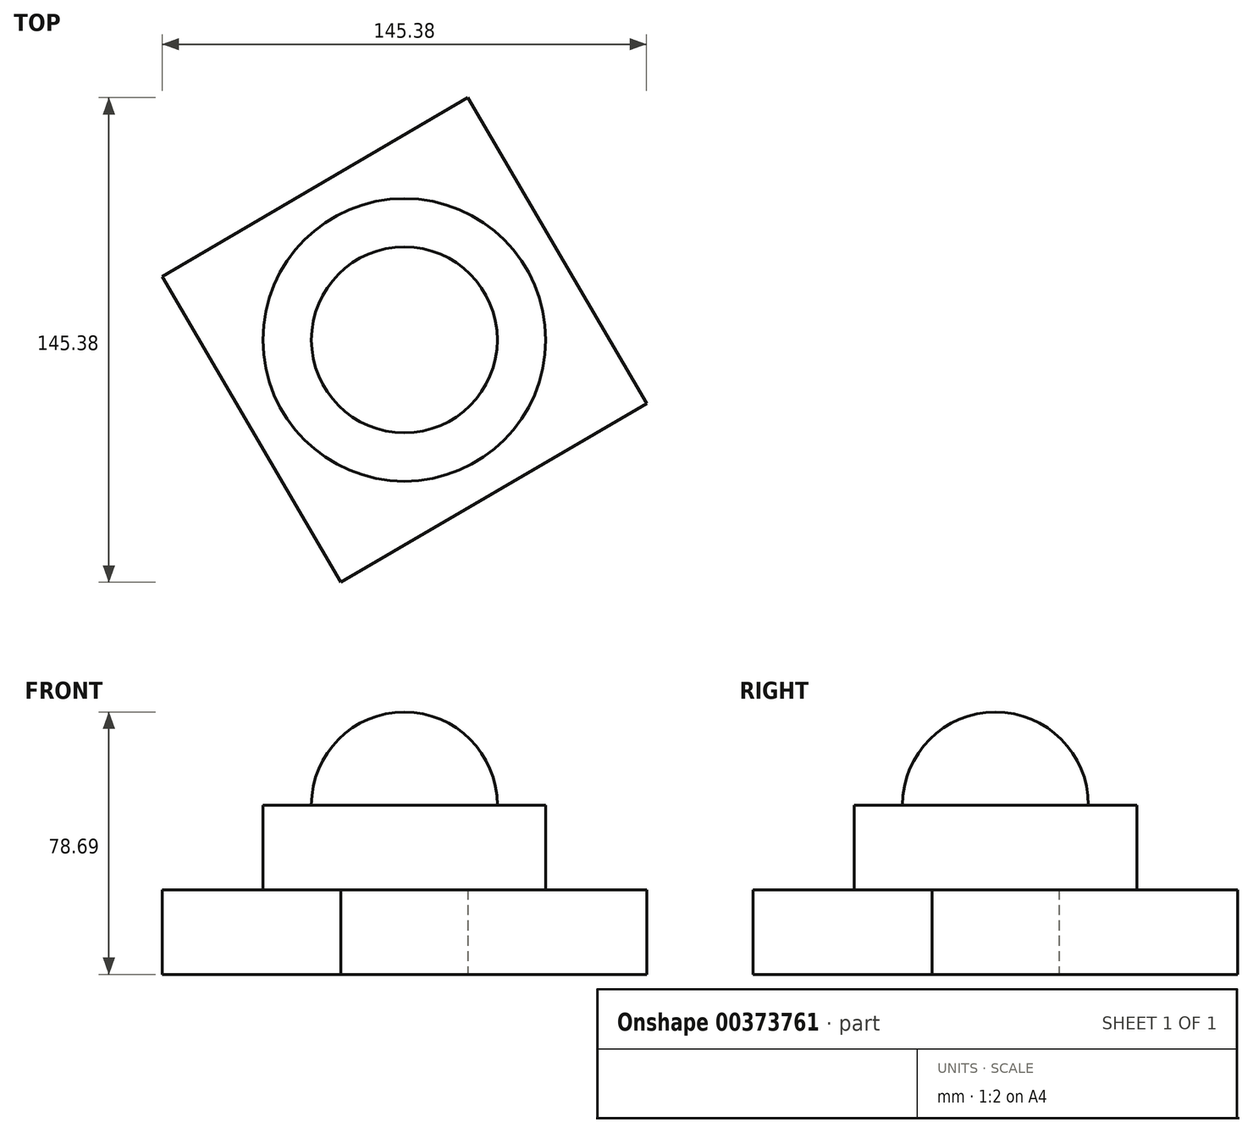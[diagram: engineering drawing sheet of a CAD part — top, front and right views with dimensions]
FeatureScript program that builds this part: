
annotation { "Feature Type Name" : "Feature", "Feature Type Description" : "" }
export const myFeature = defineFeature(function(context is Context, id is Id, definition is map)
    precondition{}
    {
        {
            var Q0;
            Q0=qCreatedBy(makeId("Top.planeOp"),FACE);
            var sketch = newSketch(context, id + "F0", { "sketchPlane" : qUnion([Q0])});
            skCircle(sketch, "E0.cCircle", {"center": v(0, 0) * mm, "radius": 53.14 * mm, "construction": true});
            skLineSegment(sketch, "E0.0", {"start": v(-72.7, 19.05) * mm, "end": v(19.05, 72.7) * mm});
            skLineSegment(sketch, "E0.1", {"start": v(19.05, 72.7) * mm, "end": v(72.7, -19.05) * mm});
            skLineSegment(sketch, "E0.2", {"start": v(72.7, -19.05) * mm, "end": v(-19.05, -72.7) * mm});
            skLineSegment(sketch, "E0.3", {"start": v(-19.05, -72.7) * mm, "end": v(-72.7, 19.05) * mm});
            skPoint(sketch, "E0.0.midPoint", {"position": v(-26.82, 45.87) * mm});
            skSolve(sketch);
        }
        {
            var Q0;
            Q0 = qSketchRegion(id + "F0", true);
            extrude(context, id + "F1", {"entities" : qUnion([Q0]), "depth" : 25.4 * mm});
        }
        {
            var Q0;
            Q0=makeQuery(id+"F1.opExtrude","CAP_FACE",FACE,{"disambiguationData":[OSD([sQuery(id+"F0.wireOp",EDGE,"E0.0"),sQuery(id+"F0.wireOp",EDGE,"E0.1"),sQuery(id+"F0.wireOp",EDGE,"E0.2"),sQuery(id+"F0.wireOp",EDGE,"E0.3")])],"isStart":false});
            var sketch = newSketch(context, id + "F2", { "sketchPlane" : qUnion([Q0])});
            skCircle(sketch, "E1", {"center": v(0, 0) * mm, "radius": 42.41 * mm});
            skSolve(sketch);
        }
        {
            var Q0;
            Q0=makeQuery(id+"F2.imprint","IMPRINT",FACE,{"disambiguationData":[TD([[makeQuery(id+"F2.imprint","IMPRINT",EDGE,{"derivedFrom":sQuery(id+"F2.wireOp",EDGE,"E1")}),1.0]])]});
            extrude(context, id + "F3", {"entities" : qUnion([Q0]), "operationType" : NewBodyOperationType.ADD, "depth" : 25.4 * mm});
        }
        {
            var Q0;
            Q0=makeQuery(id+"F3.opExtrude","CAP_FACE",FACE,{"disambiguationData":[OSD([sQuery(id+"F2.wireOp",EDGE,"E1")])],"isStart":false});
            var sketch = newSketch(context, id + "F4", { "sketchPlane" : qUnion([Q0])});
            skArc(sketch, "E2", {"start": v(0, -27.89) * mm, "mid": v(27.89, 0) * mm, "end": v(0, 27.89) * mm});
            skLineSegment(sketch, "E3", {"start": v(0, 27.89) * mm, "end": v(0, -27.89) * mm});
            skSolve(sketch);
        }
        {
            var Q0;
            Q0 = qSketchRegion(id + "F4", true);
            var Q1;
            Q1=sQuery(id+"F4.wireOp",EDGE,"E3");
            revolve(context, id + "F5", {"operationType" : NewBodyOperationType.ADD, "entities" : qUnion([Q0]), "axis" : qUnion([Q1]), "revolveType" : RevolveType.FULL});
        }
    });
